# Revit family: NA100
name_source: partatom
category: Mechanical Equipment
revit_build: Autodesk Revit 2015 (Build: 20140606_1530(x64)
units: mm (PartAtom-declared; Revit-internal decimal feet)

## types (7) — shared parameters
Apparent Load = 23 VA
Catalogue Pages = http://www.nuaire.info
Classification.Uniclass.Pr.Description = Axial flow fans
Classification.Uniclass.Pr.Number = Pr_65_67_29_05
Depth = 17 mm
Electrical Phase = 1
Fax Number = +44(0)2920-858-222
Full Load Current = 0 A
Height = 160 mm  [stored 0.524934 ft]
I&M Manual = http://www.nuaire.info
IFCExportAs = IfcFanType
Manufacturer = Nuaire
Manufacturer Name = Nuaire
Maximum Ambient Temperature = 40 °C
Nominal Motor Rating = 11 W
OmniClass Number = 23-33 31 19 11
OmniClass Title = Axial Fans
Postcode = CF83 1NA
Revit Family Last Revised = 31/10/18
Spigot Diameter = 100 mm  [stored 0.328084 ft]
Spigot Radius = 50 mm  [stored 0.164042 ft]
Telephone Number = +44(0)2920-858-200
URL = http://www.nuaire.co.uk
VAT Registration Number = 877308
Voltage = 230 V
Warranty Period = 3 Years
Weatherproof or Internal Only = Internal
Weight = 0.42 kg
Width = 160 mm  [stored 0.524934 ft]

## per-type parameters (varying)
| type | Description | Number of Connection Poles | PIR | Unit Description |
| NA100 | Wall Mounted Fan Unit | 1 | No | Wall Mounted Fan Unit |
| NA100-12 | 12V Wall Mounted Fan Unit | 1 | No | 12V Wall Mounted Fan Unit |
| NA100HT | Wall Mounted Fan Unit with Humidistat and Run on Timer | 1 | No | Wall Mounted Fan Unit with Humidistat and Run on Timer |
| NA100PC | Wall Mounted Fan Unit with Pull Cord | 1 | No | Wall Mounted Fan Unit with Pull Cord |
| NA100PIR | Wall Mounted Fan Unit with Integral PIR | 1 | Yes | Wall Mounted Fan Unit with Integral PIR |
| NA100T | Wall Mounted Fan Unit with Run on Timer | 1 | Yes | Wall Mounted Fan Unit with Run on Timer |
| NA100T-12 | 12V Wall Mounted Fan Unit with Run on Timer | 2 | Yes | 12V Wall Mounted Fan Unit with Run on Timer |

note: column(s) folded — value = type name in every type: Model, Nuaire Model Code

note: [stored X ft] marks values corroborated as IEEE doubles in the binary element streams (Revit-internal decimal feet)

## geometry (parser evidence)
native form markers: Blend x20, Sweep x6
no freeform markers — native parametric forms only
